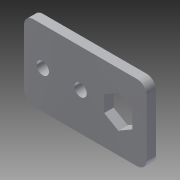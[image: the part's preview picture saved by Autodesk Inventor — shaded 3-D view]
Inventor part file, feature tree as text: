
AUTODESK INVENTOR PART (.ipt)
format: ipt  version: 2014 (Build 180170000, 170)  size: 101,888 bytes
history: native  units: in
note: dims shown in document units (in); Inventor stores cm internally (conversion verified against a paired STEP export)
features: extrude x1, fillet x1, sketch x1
ambient origin geometry x8: Origin, YZ Plane, XZ Plane, XY Plane, X Axis, Y Axis, Z Axis, Center Point
bodies: Solid1 (feature_tree)
feature tree (3):
  extrude  "Extrusion1"  Depth=1.0in
  fillet  "Fillet1"  Radius=0.163in
  sketch  "Sketch1"  dims[d0=1.625in d1=1.0in d2=0.163in d3=0.5in d4=0.25in d5=1.0in d6=0.375in d7=0.5in d8=0.125in d9=0.0in d10=0.125in d11=0.7874in d13=0.5in d14=0.3937in d16=1.0in]
